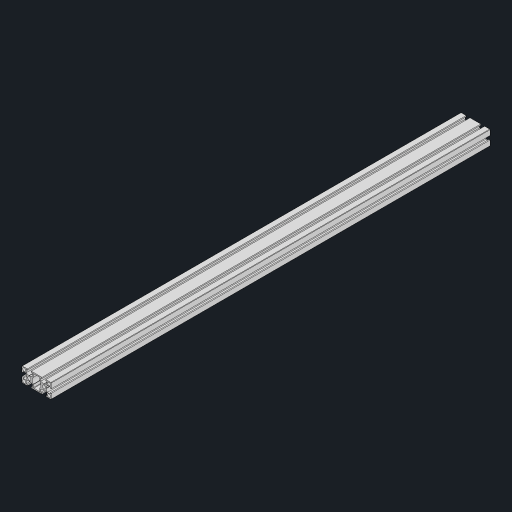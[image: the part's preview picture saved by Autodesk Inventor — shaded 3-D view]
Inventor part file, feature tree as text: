
AUTODESK INVENTOR PART (.ipt)
format: ipt  version: 2024.2 (Build 282272000, 272)  size: 229,376 bytes
history: native  units: mm
features: other x1, extrude x1, sketch x1
ambient origin geometry x8: Origin, YZ Plane, XZ Plane, XY Plane, X Axis, Y Axis, Z Axis, Center Point
bodies: Body1 (feature_tree)
feature tree (3):
  other  "솔리드1"
  extrude  "돌출1"  Depth=40.0mm
  sketch  "스케치1"
